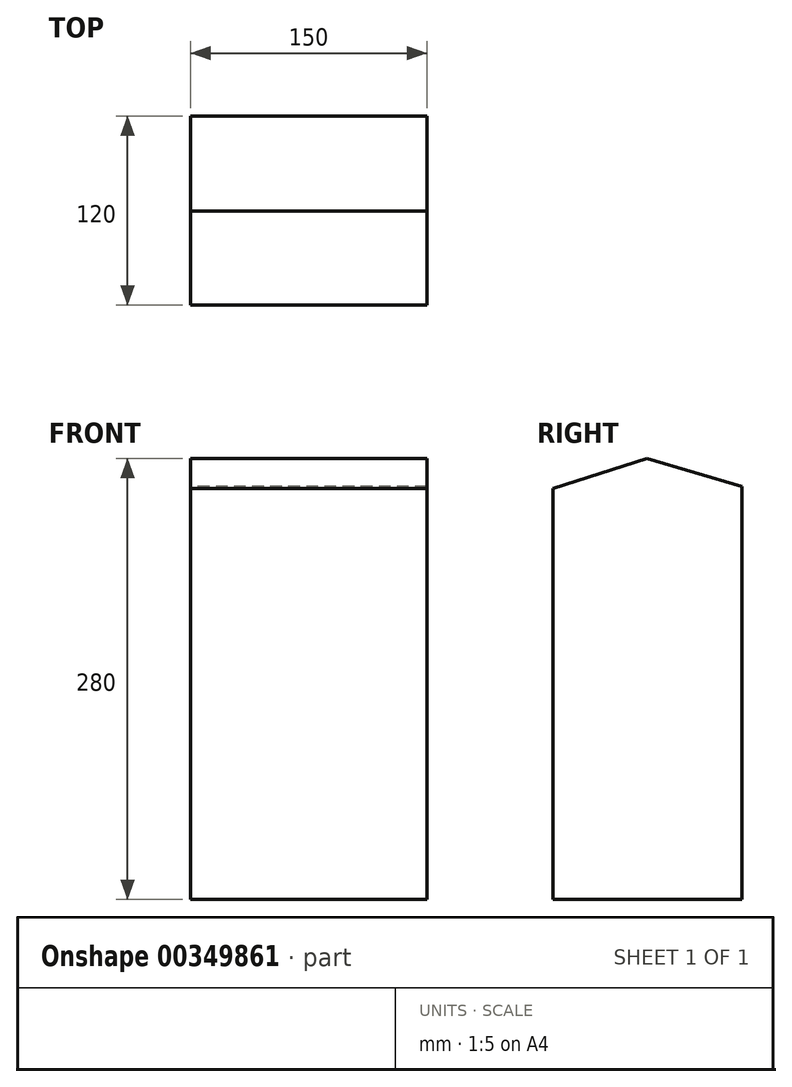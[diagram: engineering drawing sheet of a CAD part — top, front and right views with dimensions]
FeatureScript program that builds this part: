
annotation { "Feature Type Name" : "Feature", "Feature Type Description" : "" }
export const myFeature = defineFeature(function(context is Context, id is Id, definition is map)
    precondition{}
    {
        {
            var Q0;
            Q0=qCreatedBy(makeId("Top.planeOp"),FACE);
            var sketch = newSketch(context, id + "F0", { "sketchPlane" : qUnion([Q0])});
            skLineSegment(sketch, "E0.bottom", {"start": v(-76.51, 60.18) * mm, "end": v(73.49, 60.18) * mm});
            skLineSegment(sketch, "E0.top", {"start": v(-76.51, -59.82) * mm, "end": v(73.49, -59.82) * mm});
            skLineSegment(sketch, "E0.left", {"start": v(-76.51, 60.18) * mm, "end": v(-76.51, -59.82) * mm});
            skLineSegment(sketch, "E0.right", {"start": v(73.49, 60.18) * mm, "end": v(73.49, -59.82) * mm});
            skSolve(sketch);
        }
        {
            var Q0;
            Q0=makeQuery(id+"F0.imprint","IMPRINT",FACE,{"disambiguationData":[TD([[makeQuery(id+"F0.imprint","IMPRINT",EDGE,{"derivedFrom":sQuery(id+"F0.wireOp",EDGE,"E0.bottom")}),-1.0]])]});
            extrude(context, id + "F1", {"entities" : qUnion([Q0]), "depth" : 280 * mm});
        }
        {
            var Q0;
            Q0=makeQuery(id+"F1.opExtrude","SWEPT_FACE",FACE,{"disambiguationData":[OSD([sQuery(id+"F0.wireOp",EDGE,"E0.left")])]});
            var sketch = newSketch(context, id + "F2", { "sketchPlane" : qUnion([Q0])});
            skLineSegment(sketch, "E1", {"start": v(0, 280) * mm, "end": v(-60.18, 262.2) * mm});
            skLineSegment(sketch, "E2", {"start": v(0, 280) * mm, "end": v(59.82, 261.04) * mm});
            skSolve(sketch);
        }
        {
            var Q0;
            {var subQ0=sQuery(id+"F2.wireOp",EDGE,"E1");Q0=makeQuery(id+"F2.imprint","IMPRINT",FACE,{"disambiguationData":[TD([[makeQuery(id+"F2.imprint","IMPRINT",EDGE,{"derivedFrom":subQ0}),-1.0]])]});}
            var Q1;
            {var subQ0=sQuery(id+"F2.wireOp",EDGE,"E2");Q1=makeQuery(id+"F2.imprint","IMPRINT",FACE,{"disambiguationData":[TD([[makeQuery(id+"F2.imprint","IMPRINT",EDGE,{"derivedFrom":subQ0}),1.0]])]});}
            extrude(context, id + "F3", {"entities" : qUnion([Q0, Q1]), "operationType" : NewBodyOperationType.REMOVE, "endBound" : BoundingType.UP_TO_NEXT, "oppositeDirection" : true, "depth" : 25 * mm});
        }
    });
